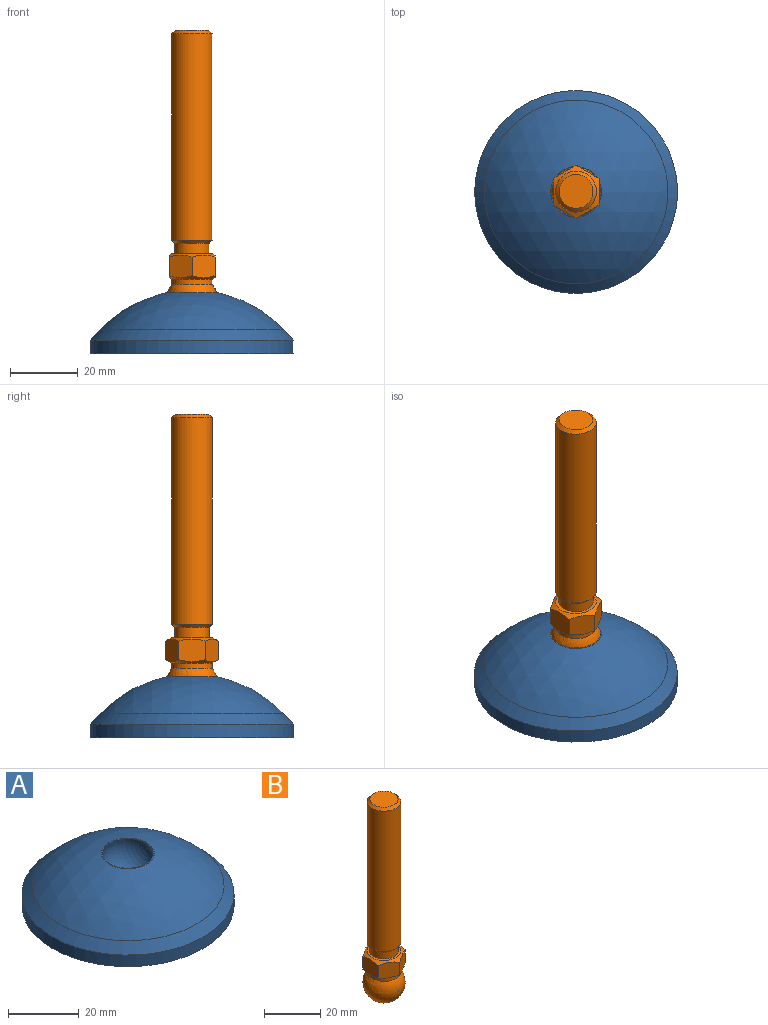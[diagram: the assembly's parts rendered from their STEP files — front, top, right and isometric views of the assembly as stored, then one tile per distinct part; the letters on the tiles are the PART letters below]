
ASSEMBLY  parts=2 mates=2
PART A: 42 faces, bbox 60x60x26.6 mm
  f0: cylinder r=30mm len=60mm, axis (0,0,1), area 754mm2, adj f4,f41
  f1: cylinder r=7.5mm len=15mm, axis (0,0,-1), area 300.2mm2, adj f5,f6,f7,f8,f9,f10,f11,f12
  f2: cylinder r=25.75mm len=51.5mm, axis (0,0,-1), area 787.4mm2, adj f31,f41
  f3: sphere r=7.5mm, area 447.7mm2, adj f30
  f4: cone r=28.59mm half-angle=43.2deg, axis (0,0,-1), area 739.3mm2, adj f0,f29
  f5: plane 15.8x15.77mm, normal (0,0,-1), area 72.8mm2, adj f1,f9,f27,f31
  f6: plane 18.41x4mm, normal (0,0,-1), area 72.8mm2, adj f1,f7,f28,f31
  f7: plane 18.31x9.82mm, normal (0,-1,0), area 109.3mm2, adj f1,f6,f31,f35
  f8: plane 18.32x9.82mm, normal (-1,0,0), area 109.4mm2, adj f1,f25,f31,f37
  f9: plane 12.95x12.95mm, normal (0.71,-0.71,0), area 109.3mm2, adj f1,f5,f31,f39
  f10: plane 18.32x9.82mm, normal (1,0,0), area 109.4mm2, adj f1,f25,f31,f36
  f11: plane 12.96x12.96mm, normal (-0.71,0.71,0), area 109.4mm2, adj f1,f23,f31,f36
  f12: plane 18.32x9.82mm, normal (1,0,0), area 109.4mm2, adj f1,f18,f31,f38
  f13: plane 12.95x12.95mm, normal (0.71,-0.71,0), area 109.3mm2, adj f1,f23,f31,f34
  f14: plane 18.33x9.82mm, normal (0,1,0), area 109.4mm2, adj f1,f24,f31,f34
  f15: plane 18.31x9.82mm, normal (0,-1,0), area 109.3mm2, adj f1,f24,f31,f32
  f16: plane 12.96x12.96mm, normal (-0.71,-0.71,0), area 109.4mm2, adj f1,f17,f31,f38
  f17: plane 15.78x15.78mm, normal (0,0,-1), area 72.8mm2, adj f1,f16,f19,f31
  f18: plane 18.4x4mm, normal (0,0,-1), area 72.8mm2, adj f1,f12,f26,f31
  f19: plane 12.96x12.96mm, normal (0.71,0.71,0), area 109.4mm2, adj f1,f17,f31,f32
  f20: plane 12.96x12.96mm, normal (0.71,0.71,0), area 109.4mm2, adj f1,f21,f31,f37
  f21: plane 15.78x15.78mm, normal (0,0,-1), area 72.8mm2, adj f1,f20,f22,f31
  f22: plane 12.96x12.96mm, normal (-0.71,-0.71,0), area 109.4mm2, adj f1,f21,f31,f33
  f23: plane 15.8x15.77mm, normal (0,0,-1), area 72.8mm2, adj f1,f11,f13,f31
  f24: plane 18.41x4mm, normal (0,0,-1), area 72.8mm2, adj f1,f14,f15,f31
  f25: plane 18.4x4mm, normal (0,0,-1), area 72.8mm2, adj f1,f8,f10,f31
  f26: plane 18.32x9.82mm, normal (-1,0,0), area 109.4mm2, adj f1,f18,f31,f39
  f27: plane 12.96x12.96mm, normal (-0.71,0.71,0), area 109.4mm2, adj f1,f5,f31,f35
  f28: plane 18.33x9.82mm, normal (0,1,0), area 109.4mm2, adj f1,f6,f31,f33
  f29: sphere r=37.29mm, area 2577.2mm2, adj f4,f30
  f30: plane 15x15mm, normal (0,0,1), area 12.6mm2, adj f3,f29
  f31: sphere r=34.79mm, area 1573.6mm2, adj f2,f5,f6,f7,f8,f9,f10,f11
  f32: sphere r=10mm, area 18.5mm2, adj f1,f15,f19,f31
  f33: sphere r=10mm, area 18mm2, adj f1,f22,f28,f31
  f34: sphere r=10mm, area 18.4mm2, adj f1,f13,f14,f31
  f35: sphere r=10mm, area 18.2mm2, adj f1,f7,f27,f31
  f36: sphere r=10mm, area 17.9mm2, adj f1,f10,f11,f31
  f37: sphere r=10mm, area 18.3mm2, adj f1,f8,f20,f31
  f38: sphere r=10mm, area 18.3mm2, adj f1,f12,f16,f31
  f39: sphere r=10mm, area 18.6mm2, adj f1,f9,f26,f31
  f40: plane 15x15mm, normal (0,0,-1), area 176.7mm2, adj f1
  f41: plane 60x60mm, normal (0,0,-1), area 744.4mm2, adj f0,f2
PART B: 16 faces, bbox 15.7x15.7x87.1 mm
  f0: cone r=5.5mm half-angle=45deg, axis (0,0,-1), area 48.9mm2, adj f1,f15
  f1: cylinder r=6mm len=61.07mm, axis (0,0,1), area 2302.4mm2, adj f0,f2
  f2: cone r=5.54mm half-angle=45deg, axis (0,0,1), area 45.6mm2, adj f1,f3
  f3: cylinder r=5.07mm len=10.15mm, axis (0,0,1), area 95.6mm2, adj f2,f14
  f4: cone r=6.92mm half-angle=60deg, axis (0,0,-1), area 54.3mm2, adj f8,f9,f10,f11,f12,f13,f14
  f5: cone r=6.92mm half-angle=60deg, axis (0,0,1), area 54.3mm2, adj f6,f8,f9,f10,f11,f12,f13
  f6: cylinder r=6mm len=12mm, axis (0,0,1), area 56.5mm2, adj f5,f7
  f7: sphere r=7.5mm, area 565.5mm2, adj f6
  f8: plane 7.26x6.8mm, normal (-0.5,0.87,0), area 49.2mm2, adj f4,f5,f11,f12
  f9: plane 7.26x6.8mm, normal (0.5,-0.87,0), area 49.2mm2, adj f4,f5,f10,f13
  f10: plane 7.85x6.68mm, normal (1,0,0), area 49.2mm2, adj f4,f5,f9,f11
  f11: plane 7.26x6.8mm, normal (0.5,0.87,0), area 49.2mm2, adj f4,f5,f8,f10
  f12: plane 7.85x6.68mm, normal (-1,0,0), area 49.2mm2, adj f4,f5,f8,f13
  f13: plane 7.26x6.8mm, normal (-0.5,-0.87,0), area 49.2mm2, adj f4,f5,f9,f12
  f14: plane 12x12mm, normal (0,0,1), area 32.2mm2, adj f3,f4
  f15: plane 10x10mm, normal (0,0,1), area 78.5mm2, adj f0
PLACE A t=(-83.17,-10.73,-0.14)mm
PLACE B t=(-83.17,-10.73,-0.14)mm
MATE parallel A.f0 <-> B.f0  axis (0,0,-1) through (-83.17,-10.73,-0.14)mm
MATE ball B.f6 <-> A.f0  axis (0,0,1) through (-83.17,-10.73,15.86)mm
